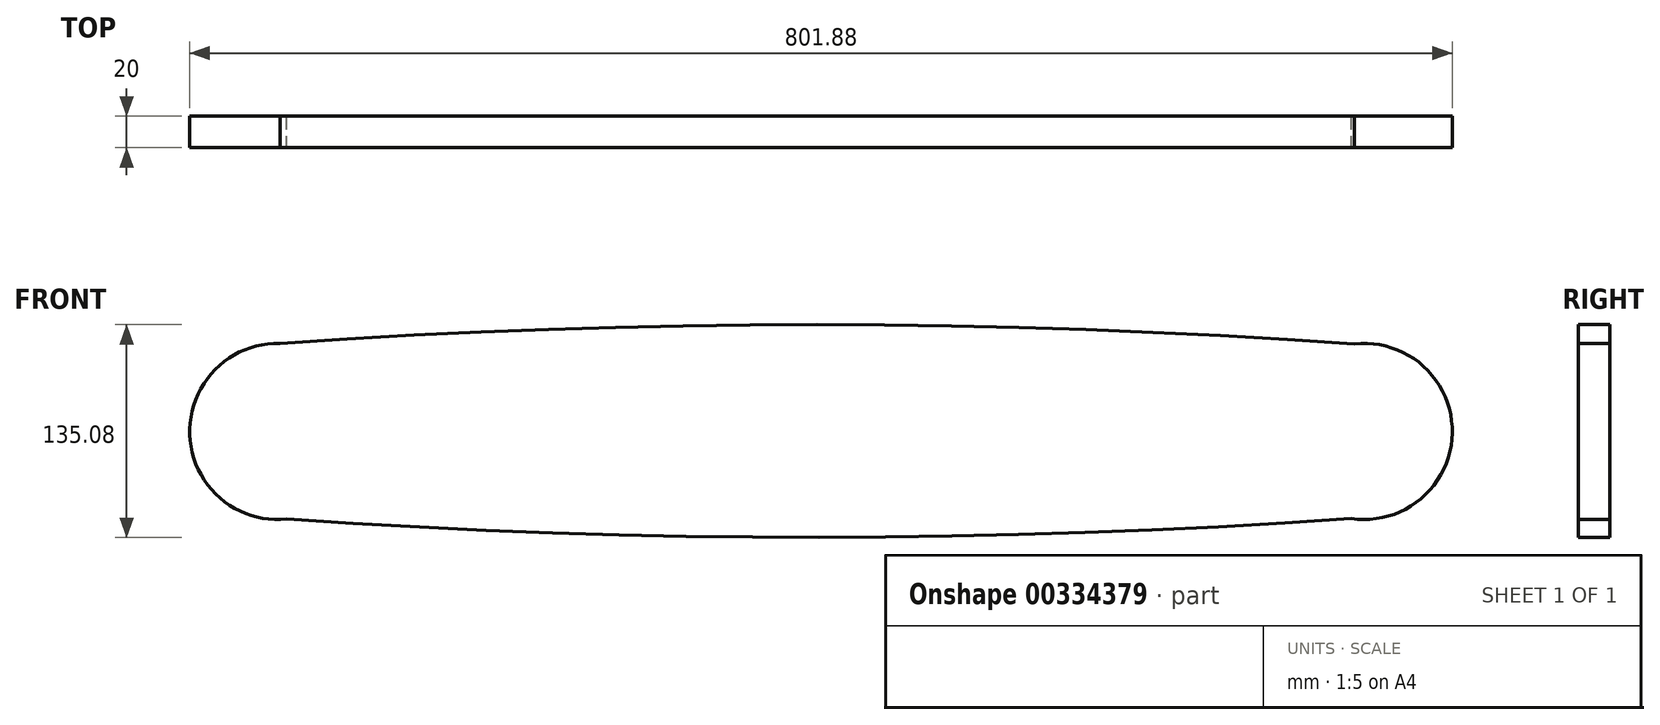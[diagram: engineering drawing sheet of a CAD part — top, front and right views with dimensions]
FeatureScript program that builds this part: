
annotation { "Feature Type Name" : "Feature", "Feature Type Description" : "" }
export const myFeature = defineFeature(function(context is Context, id is Id, definition is map)
    precondition{}
    {
        {
            var Q0;
            Q0=qCreatedBy(makeId("Front.planeOp"),FACE);
            var sketch = newSketch(context, id + "F0", { "sketchPlane" : qUnion([Q0])});
            skCircle(sketch, "E0", {"center": v(-345, 0) * mm, "radius": 55.94 * mm});
            skCircle(sketch, "E1", {"center": v(345, 0) * mm, "radius": 55.94 * mm});
            skLineSegment(sketch, "E2", {"start": v(-345, 0) * mm, "end": v(345, 0) * mm});
            skArc(sketch, "E3", {"start": v(-339.36, -55.66) * mm, "mid": v(-1.3, -67.3) * mm, "end": v(336.77, -55.34) * mm});
            skArc(sketch, "E4", {"start": v(338.86, 55.6) * mm, "mid": v(-2.37, 67.79) * mm, "end": v(-343.61, 55.93) * mm});
            skSolve(sketch);
        }
        {
            var Q0;
            {var subQ0=sQuery(id+"F0.wireOp",EDGE,"E0");var subQ1=makeQuery(id+"F0.imprint","INTERSECT",VERTEX,{"derivedFrom":[subQ0,sQuery(id+"F0.wireOp",EDGE,"E4")]});Q0=makeQuery(id+"F0.imprint","IMPRINT",FACE,{"disambiguationData":[TD([[makeQuery(id+"F0.imprint","IMPRINT",EDGE,{"disambiguationData":[TD([[subQ1,1.0]])],"derivedFrom":subQ0}),1.0]])]});}
            var Q1;
            {var subQ0=sQuery(id+"F0.wireOp",EDGE,"E4");Q1=makeQuery(id+"F0.imprint","IMPRINT",FACE,{"disambiguationData":[TD([[makeQuery(id+"F0.imprint","IMPRINT",EDGE,{"derivedFrom":subQ0}),1.0]])]});}
            var Q2;
            {var subQ0=sQuery(id+"F0.wireOp",EDGE,"E3");Q2=makeQuery(id+"F0.imprint","IMPRINT",FACE,{"disambiguationData":[TD([[makeQuery(id+"F0.imprint","IMPRINT",EDGE,{"derivedFrom":subQ0}),1.0]])]});}
            var Q3;
            {var subQ0=sQuery(id+"F0.wireOp",EDGE,"E1");var subQ1=makeQuery(id+"F0.imprint","INTERSECT",VERTEX,{"derivedFrom":[subQ0,sQuery(id+"F0.wireOp",EDGE,"E4")]});Q3=makeQuery(id+"F0.imprint","IMPRINT",FACE,{"disambiguationData":[TD([[makeQuery(id+"F0.imprint","IMPRINT",EDGE,{"disambiguationData":[TD([[subQ1,-1.0]])],"derivedFrom":subQ0}),1.0]])]});}
            extrude(context, id + "F1", {"entities" : qUnion([Q0, Q1, Q2, Q3]), "depth" : 20 * mm});
        }
    });
